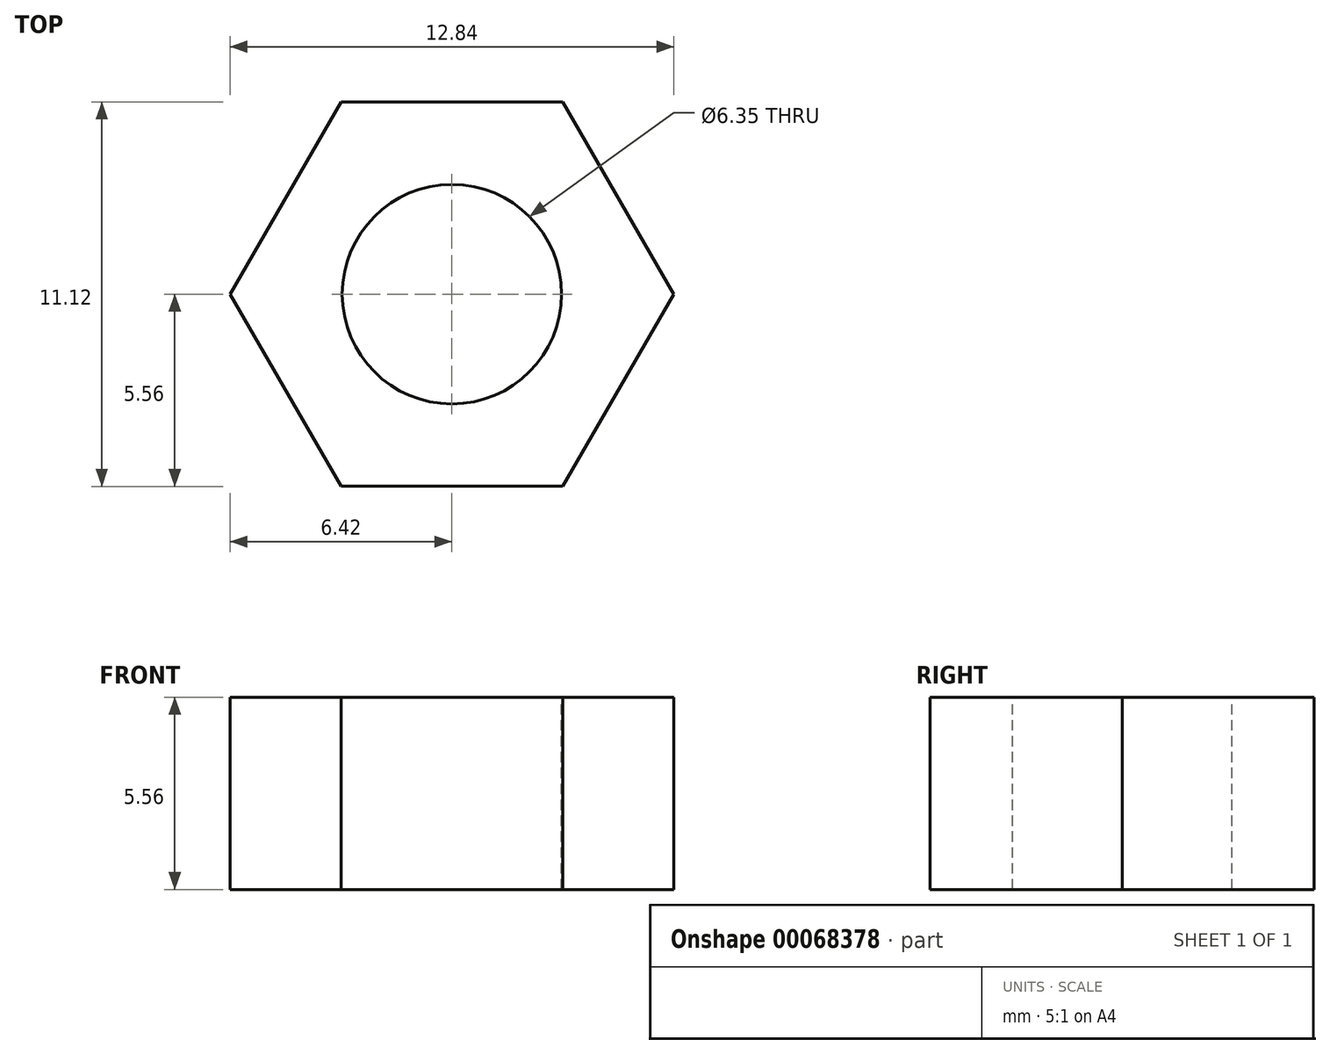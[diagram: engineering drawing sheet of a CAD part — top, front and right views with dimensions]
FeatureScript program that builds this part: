
annotation { "Feature Type Name" : "Feature", "Feature Type Description" : "" }
export const myFeature = defineFeature(function(context is Context, id is Id, definition is map)
    precondition{}
    {
        {
            var Q0;
            Q0=qCreatedBy(makeId("Top.planeOp"),FACE);
            var sketch = newSketch(context, id + "F0", { "sketchPlane" : qUnion([Q0])});
            skCircle(sketch, "E0.cCircle", {"center": v(0, 0) * mm, "radius": 5.56 * mm, "construction": true});
            skLineSegment(sketch, "E0.0", {"start": v(3.2, -5.56) * mm, "end": v(-3.2, -5.56) * mm});
            skLineSegment(sketch, "E0.1", {"start": v(-3.2, -5.56) * mm, "end": v(-6.42, 0) * mm});
            skLineSegment(sketch, "E0.2", {"start": v(-6.42, 0) * mm, "end": v(-3.2, 5.56) * mm});
            skLineSegment(sketch, "E0.3", {"start": v(-3.2, 5.56) * mm, "end": v(3.2, 5.56) * mm});
            skLineSegment(sketch, "E0.4", {"start": v(3.2, 5.56) * mm, "end": v(6.42, 0) * mm});
            skLineSegment(sketch, "E0.5", {"start": v(6.42, 0) * mm, "end": v(3.2, -5.56) * mm});
            skPoint(sketch, "E0.0.midPoint", {"position": v(0, -5.56) * mm});
            skSolve(sketch);
        }
        {
            var Q0;
            Q0=makeQuery(id+"F0.imprint","IMPRINT",FACE,{"disambiguationData":[TD([[makeQuery(id+"F0.imprint","IMPRINT",EDGE,{"derivedFrom":sQuery(id+"F0.wireOp",EDGE,"E0.0")}),-1.0]])]});
            extrude(context, id + "F1", {"entities" : qUnion([Q0]), "depth" : 5.56 * mm});
        }
        {
            var Q0;
            Q0=makeQuery(id+"F1.opExtrude","CAP_FACE",FACE,{"disambiguationData":[OSD([sQuery(id+"F0.wireOp",EDGE,"E0.0"),sQuery(id+"F0.wireOp",EDGE,"E0.1"),sQuery(id+"F0.wireOp",EDGE,"E0.2"),sQuery(id+"F0.wireOp",EDGE,"E0.3"),sQuery(id+"F0.wireOp",EDGE,"E0.4"),sQuery(id+"F0.wireOp",EDGE,"E0.5")])],"isStart":false});
            var sketch = newSketch(context, id + "F2", { "sketchPlane" : qUnion([Q0])});
            skCircle(sketch, "E1", {"center": v(0, 0) * mm, "radius": 3.18 * mm});
            skSolve(sketch);
        }
        {
            var Q0;
            Q0=makeQuery(id+"F2.imprint","IMPRINT",FACE,{"disambiguationData":[TD([[makeQuery(id+"F2.imprint","IMPRINT",EDGE,{"derivedFrom":sQuery(id+"F2.wireOp",EDGE,"E1")}),1.0]])]});
            extrude(context, id + "F3", {"entities" : qUnion([Q0]), "operationType" : NewBodyOperationType.REMOVE, "oppositeDirection" : true, "depth" : 6.1 * mm});
        }
    });
